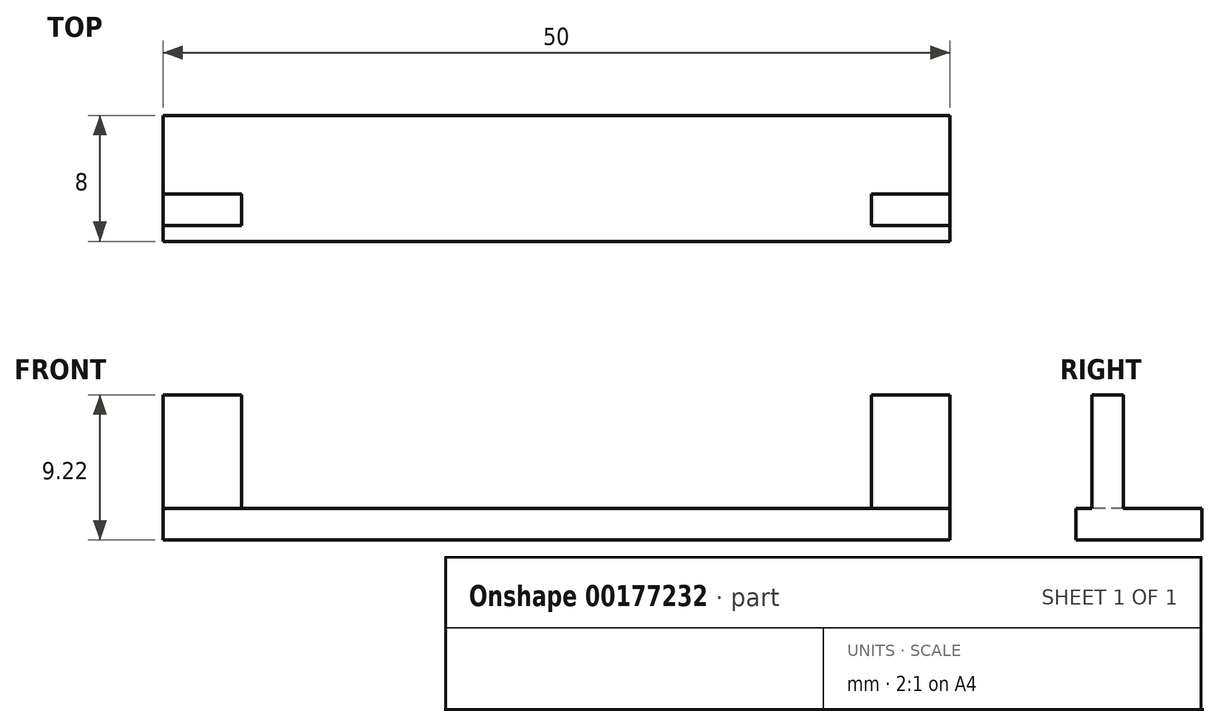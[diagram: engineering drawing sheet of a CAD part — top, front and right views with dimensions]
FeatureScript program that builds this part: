
annotation { "Feature Type Name" : "Feature", "Feature Type Description" : "" }
export const myFeature = defineFeature(function(context is Context, id is Id, definition is map)
    precondition{}
    {
        {
            var Q0;
            Q0=qCreatedBy(makeId("Right.planeOp"),FACE);
            var sketch = newSketch(context, id + "F0", { "sketchPlane" : qUnion([Q0])});
            skLineSegment(sketch, "E0.bottom", {"start": v(-4.9, 0) * mm, "end": v(3.1, 0) * mm});
            skLineSegment(sketch, "E0.top", {"start": v(-4.9, 2) * mm, "end": v(3.1, 2) * mm});
            skLineSegment(sketch, "E0.left", {"start": v(-4.9, 0) * mm, "end": v(-4.9, 2) * mm});
            skLineSegment(sketch, "E0.right", {"start": v(3.1, 0) * mm, "end": v(3.1, 2) * mm});
            skLineSegment(sketch, "E1.bottom", {"start": v(-4.9, 2) * mm, "end": v(-1.9, 2) * mm});
            skLineSegment(sketch, "E1.top", {"start": v(-3.9, 9.22) * mm, "end": v(-1.9, 9.22) * mm});
            skLineSegment(sketch, "E1.right", {"start": v(-1.9, 2) * mm, "end": v(-1.9, 9.22) * mm});
            skLineSegment(sketch, "E2.bottom", {"start": v(3.1, 2) * mm, "end": v(1.1, 2) * mm});
            skLineSegment(sketch, "E2.top", {"start": v(3.1, 9.22) * mm, "end": v(1.1, 9.22) * mm});
            skLineSegment(sketch, "E2.left", {"start": v(3.1, 2) * mm, "end": v(3.1, 9.22) * mm});
            skLineSegment(sketch, "E2.right", {"start": v(1.1, 2) * mm, "end": v(1.1, 9.22) * mm});
            skLineSegment(sketch, "E3", {"start": v(-3.9, 9.22) * mm, "end": v(-3.9, 2) * mm});
            skSolve(sketch);
        }
        {
            var Q0;
            Q0=makeQuery(id+"F0.imprint","IMPRINT",FACE,{"disambiguationData":[TD([[makeQuery(id+"F0.imprint","IMPRINT",EDGE,{"derivedFrom":sQuery(id+"F0.wireOp",EDGE,"E0.bottom")}),1.0]])]});
            var Q1;
            Q1=makeQuery(id+"F0.imprint","IMPRINT",FACE,{"disambiguationData":[TD([[makeQuery(id+"F0.imprint","IMPRINT",EDGE,{"derivedFrom":sQuery(id+"F0.wireOp",EDGE,"E1.top")}),-1.0]])]});
            var Q2;
            Q2=makeQuery(id+"F0.imprint","IMPRINT",FACE,{"disambiguationData":[TD([[makeQuery(id+"F0.imprint","IMPRINT",EDGE,{"derivedFrom":sQuery(id+"F0.wireOp",EDGE,"E2.bottom")}),-1.0]])]});
            extrude(context, id + "F1", {"entities" : qUnion([Q0, Q1, Q2]), "depth" : 50 * mm});
        }
        {
            var Q0;
            Q0=qCreatedBy(makeId("Front.planeOp"),FACE);
            var sketch = newSketch(context, id + "F2", { "sketchPlane" : qUnion([Q0])});
            skLineSegment(sketch, "E4.bottom", {"start": v(5, 2) * mm, "end": v(45, 2) * mm});
            skLineSegment(sketch, "E4.top", {"start": v(5, 12.3) * mm, "end": v(45, 12.3) * mm});
            skLineSegment(sketch, "E4.left", {"start": v(5, 2) * mm, "end": v(5, 12.3) * mm});
            skLineSegment(sketch, "E4.right", {"start": v(45, 2) * mm, "end": v(45, 12.3) * mm});
            skSolve(sketch);
        }
        {
            var Q0;
            Q0=makeQuery(id+"F2.imprint","IMPRINT",FACE,{"disambiguationData":[TD([[makeQuery(id+"F2.imprint","IMPRINT",EDGE,{"derivedFrom":sQuery(id+"F2.wireOp",EDGE,"E4.bottom")}),1.0]])]});
            extrude(context, id + "F3", {"entities" : qUnion([Q0]), "operationType" : NewBodyOperationType.REMOVE, "endBound" : BoundingType.SYMMETRIC, "oppositeDirection" : true, "depth" : 25 * mm});
        }
        {
            var Q0;
            Q0=makeQuery(id+"F1.opExtrude","SWEPT_BODY",BODY,{"disambiguationData":[OSD([sQuery(id+"F0.wireOp",EDGE,"E0.bottom"),sQuery(id+"F0.wireOp",EDGE,"E0.top"),sQuery(id+"F0.wireOp",EDGE,"E0.left"),sQuery(id+"F0.wireOp",EDGE,"E0.right"),sQuery(id+"F0.wireOp",EDGE,"E1.bottom"),sQuery(id+"F0.wireOp",EDGE,"E1.top"),sQuery(id+"F0.wireOp",EDGE,"E1.right"),sQuery(id+"F0.wireOp",EDGE,"E2.top"),sQuery(id+"F0.wireOp",EDGE,"E2.left"),sQuery(id+"F0.wireOp",EDGE,"E2.right"),sQuery(id+"F0.wireOp",EDGE,"E3")])]});
            transform(context, id + "F4", {"entities" : qUnion([Q0]), "transformType" : TransformType.TRANSLATION_3D, "dx" : -25 * mm, "dy" : 0 * mm, "dz" : 0 * mm, "makeCopy" : false});
        }
    });
